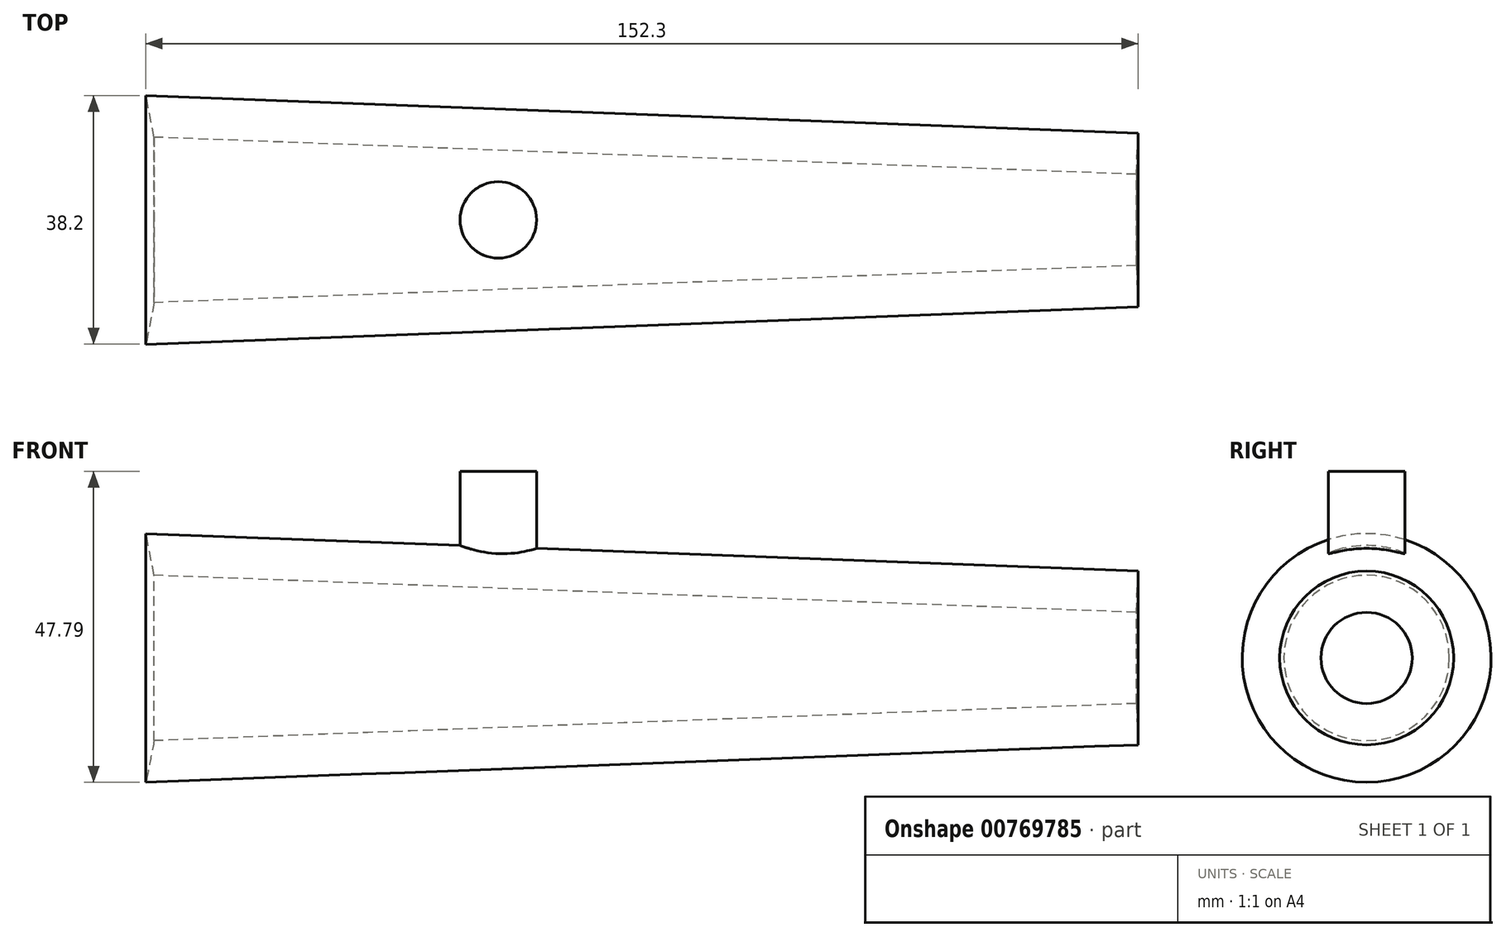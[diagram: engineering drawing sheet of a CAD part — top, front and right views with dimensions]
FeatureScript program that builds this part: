
annotation { "Feature Type Name" : "Feature", "Feature Type Description" : "" }
export const myFeature = defineFeature(function(context is Context, id is Id, definition is map)
    precondition{}
    {
        {
            var Q0;
            Q0=qCreatedBy(makeId("Front.planeOp"),FACE);
            var sketch = newSketch(context, id + "F0", { "sketchPlane" : qUnion([Q0])});
            skLineSegment(sketch, "E0", {"start": v(-24.37, -9.59) * mm, "end": v(127.93, -15.34) * mm});
            skLineSegment(sketch, "E1", {"start": v(127.93, -15.34) * mm, "end": v(127.69, -21.69) * mm});
            skLineSegment(sketch, "E2", {"start": v(127.69, -21.69) * mm, "end": v(-23.1, -15.99) * mm});
            skLineSegment(sketch, "E3", {"start": v(-23.1, -15.99) * mm, "end": v(-24.37, -9.59) * mm});
            skLineSegment(sketch, "E4", {"start": v(0, 14.58) * mm, "end": v(0, -15.3) * mm});
            skLineSegment(sketch, "E5", {"start": v(127.69, -28.69) * mm, "end": v(-23.2, -28.69) * mm});
            skSolve(sketch);
        }
        {
            var Q0;
            {var subQ2=sQuery(id+"F0.wireOp",EDGE,"E1");Q0=makeQuery(id+"F0.imprint","IMPRINT",FACE,{"disambiguationData":[TD([[makeQuery(id+"F0.imprint","IMPRINT",EDGE,{"derivedFrom":subQ2}),-1.0]])]});}
            var Q1;
            Q1=sQuery(id+"F0.wireOp",EDGE,"E5");
            revolve(context, id + "F1", {"surfaceOperationType" : NewSurfaceOperationType.NEW, "entities" : qUnion([Q0]), "axis" : qUnion([Q1]), "revolveType" : RevolveType.FULL});
        }
        {
            var Q0;
            Q0=qCreatedBy(makeId("Top.planeOp"),FACE);
            var sketch = newSketch(context, id + "F2", { "sketchPlane" : qUnion([Q0])});
            skCircle(sketch, "E6", {"center": v(29.73, 0) * mm, "radius": 5.86 * mm});
            skSolve(sketch);
        }
        {
            var Q0;
            Q0=makeQuery(id+"F2.imprint","IMPRINT",FACE,{"disambiguationData":[TD([[makeQuery(id+"F2.imprint","IMPRINT",EDGE,{"derivedFrom":sQuery(id+"F2.wireOp",EDGE,"E6")}),1.0]])]});
            extrude(context, id + "F3", {"entities" : qUnion([Q0]), "operationType" : NewBodyOperationType.ADD, "endBound" : BoundingType.UP_TO_NEXT, "oppositeDirection" : true, "depth" : 25.4 * mm, "offsetDistance" : 25.4 * mm});
        }
    });
